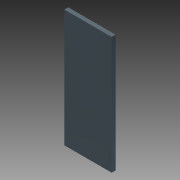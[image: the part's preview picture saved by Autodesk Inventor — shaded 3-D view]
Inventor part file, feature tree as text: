
AUTODESK INVENTOR PART (.ipt)
format: ipt  version: 2015 (Build 190159000, 159)  size: 71,168 bytes
history: native  units: mm
features: extrude x1, sketch x1
ambient origin geometry x8: Origin, YZ Plane, XZ Plane, XY Plane, X Axis, Y Axis, Z Axis, Center Point
bodies: Solid1 (feature_tree)
feature tree (2):
  extrude  "Extrusion1"  Depth=38.175mm
  sketch  "Sketch1"  dims[d0=94.763mm d1=38.175mm d2=3.175mm d3=0.0mm]
